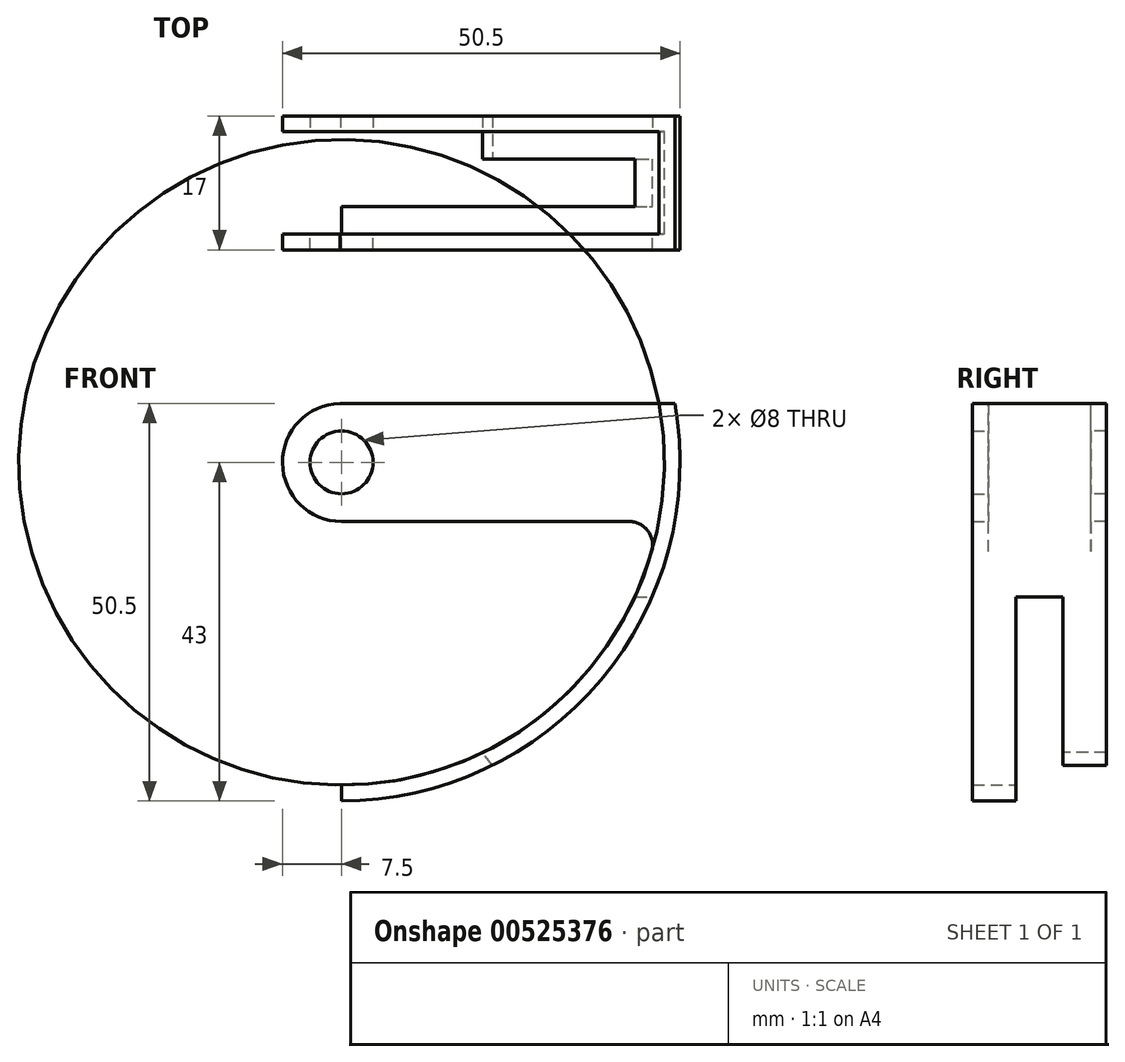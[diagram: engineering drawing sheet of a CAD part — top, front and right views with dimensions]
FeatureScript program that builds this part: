
annotation { "Feature Type Name" : "Feature", "Feature Type Description" : "" }
export const myFeature = defineFeature(function(context is Context, id is Id, definition is map)
    precondition{}
    {
        {
            var Q0;
            Q0=qCreatedBy(makeId("Front.planeOp"),FACE);
            var sketch = newSketch(context, id + "F0", { "sketchPlane" : qUnion([Q0])});
            skCircle(sketch, "E0", {"center": v(0, 0) * mm, "radius": 7.5 * mm});
            skLineSegment(sketch, "E1", {"start": v(0, 7.5) * mm, "end": v(42.34, 7.5) * mm});
            skLineSegment(sketch, "E2", {"start": v(0, -17) * mm, "end": v(32.65, -17) * mm});
            skLineSegment(sketch, "E3", {"start": v(37.28, -17.06) * mm, "end": v(39.47, -17.06) * mm});
            skArc(sketch, "E4", {"start": v(40.3, 7.5) * mm, "mid": v(-40.7, 5.02) * mm, "end": v(37.28, -17.06) * mm});
            skArc(sketch, "E5", {"start": v(37.28, -17.06) * mm, "mid": v(40.7, -5.02) * mm, "end": v(40.3, 7.5) * mm});
            skArc(sketch, "E6", {"start": v(39.47, -17.06) * mm, "mid": v(42.7, -5) * mm, "end": v(42.34, 7.5) * mm});
            skArc(sketch, "E7", {"start": v(42.34, 7.5) * mm, "mid": v(-42.7, 5) * mm, "end": v(39.47, -17.06) * mm});
            skSolve(sketch);
        }
        {
            var Q0;
            Q0=makeQuery(id+"F0.imprint","IMPRINT",FACE,{"disambiguationData":[TD([[makeQuery(id+"F0.imprint","IMPRINT",EDGE,{"derivedFrom":sQuery(id+"F0.wireOp",EDGE,"E3")}),1.0]])]});
            extrude(context, id + "F1", {"entities" : qUnion([Q0]), "depth" : 3 * mm, "offsetDistance" : 25.4 * mm});
        }
        {
            var Q0;
            Q0=makeQuery(id+"F1.opExtrude","SWEPT_BODY",BODY,{"disambiguationData":[OSD([sQuery(id+"F0.wireOp",EDGE,"E1"),sQuery(id+"F0.wireOp",EDGE,"E3"),sQuery(id+"F0.wireOp",EDGE,"E5"),sQuery(id+"F0.wireOp",EDGE,"E6")])]});
            var Q1;
            Q1=qCreatedBy(makeId("Front.planeOp"),FACE);
            mirror(context, id + "F2", {"operationType" : NewBodyOperationType.ADD, "entities" : qUnion([Q0]), "mirrorPlane" : qUnion([Q1])});
        }
        {
            var Q0;
            Q0=makeQuery(id+"F1.opExtrude","CAP_FACE",FACE,{"disambiguationData":[OSD([sQuery(id+"F0.wireOp",EDGE,"E1"),sQuery(id+"F0.wireOp",EDGE,"E3"),sQuery(id+"F0.wireOp",EDGE,"E5"),sQuery(id+"F0.wireOp",EDGE,"E6")])],"isStart":false});
            var sketch = newSketch(context, id + "F3", { "sketchPlane" : qUnion([Q0])});
            skCircle(sketch, "E8", {"center": v(0, 0) * mm, "radius": 7.5 * mm});
            skLineSegment(sketch, "E9", {"start": v(0, 7.5) * mm, "end": v(42.34, 7.5) * mm});
            skLineSegment(sketch, "E10", {"start": v(-7.6, -13.58) * mm, "end": v(25.06, -13.58) * mm});
            skLineSegment(sketch, "E11", {"start": v(37.28, -17.06) * mm, "end": v(39.47, -17.06) * mm});
            skArc(sketch, "E12", {"start": v(40.3, 7.5) * mm, "mid": v(-40.7, 5.02) * mm, "end": v(37.28, -17.06) * mm});
            skArc(sketch, "E13", {"start": v(37.28, -17.06) * mm, "mid": v(40.7, -5.02) * mm, "end": v(40.3, 7.5) * mm});
            skArc(sketch, "E14", {"start": v(39.47, -17.06) * mm, "mid": v(42.7, -5) * mm, "end": v(42.34, 7.5) * mm});
            skArc(sketch, "E15", {"start": v(42.34, 7.5) * mm, "mid": v(-42.7, 5) * mm, "end": v(39.47, -17.06) * mm});
            skLineSegment(sketch, "E16", {"start": v(0, -41) * mm, "end": v(0, -43) * mm});
            skSolve(sketch);
        }
        {
            var Q0;
            {var subQ0=sQuery(id+"F3.wireOp",EDGE,"E11");Q0=makeQuery(id+"F3.imprint","IMPRINT",FACE,{"disambiguationData":[TD([[makeQuery(id+"F3.imprint","IMPRINT",EDGE,{"derivedFrom":subQ0}),-1.0]])]});}
            var Q1;
            Q1=makeQuery(id+"F3.imprint","IMPRINT",FACE,{"disambiguationData":[TD([[makeQuery(id+"F3.imprint","IMPRINT",EDGE,{"derivedFrom":sQuery(id+"F3.wireOp",EDGE,"E11")}),1.0]])]});
            extrude(context, id + "F4", {"entities" : qUnion([Q0, Q1]), "operationType" : NewBodyOperationType.ADD, "depth" : 3.5 * mm, "offsetDistance" : 25.4 * mm});
        }
        {
            var Q0;
            Q0=makeQuery(id+"F4.opExtrude","CAP_FACE",FACE,{"disambiguationData":[OSD([sQuery(id+"F3.wireOp",EDGE,"E9"),sQuery(id+"F3.wireOp",EDGE,"E12"),sQuery(id+"F3.wireOp",EDGE,"E13"),sQuery(id+"F3.wireOp",EDGE,"E14"),sQuery(id+"F3.wireOp",EDGE,"E15"),sQuery(id+"F3.wireOp",EDGE,"E16")])],"isStart":false});
            var sketch = newSketch(context, id + "F5", { "sketchPlane" : qUnion([Q0])});
            skArc(sketch, "E17", {"start": v(37.28, -17.06) * mm, "mid": v(38.45, -14.24) * mm, "end": v(39.4, -11.33) * mm});
            skArc(sketch, "E18", {"start": v(39.47, -17.06) * mm, "mid": v(42.7, -5) * mm, "end": v(42.34, 7.5) * mm});
            skLineSegment(sketch, "E19", {"start": v(0, -7.5) * mm, "end": v(36.52, -7.5) * mm});
            skArc(sketch, "E20", {"start": v(-0.2, 7.5) * mm, "mid": v(-7.5, -0.1) * mm, "end": v(0, -7.5) * mm});
            skCircle(sketch, "E21", {"center": v(0, 0) * mm, "radius": 4 * mm});
            skLineSegment(sketch, "E22", {"start": v(40.3, -7.5) * mm, "end": v(40.3, -7.5) * mm});
            skArc(sketch, "E23.filletArc", {"start": v(39.4, -11.33) * mm, "mid": v(38.92, -8.7) * mm, "end": v(36.52, -7.5) * mm});
            skArc(sketch, "E24", {"start": v(0, -41) * mm, "mid": v(22.15, -34.5) * mm, "end": v(37.28, -17.06) * mm});
            skArc(sketch, "E25", {"start": v(0, -43) * mm, "mid": v(23.61, -35.94) * mm, "end": v(39.47, -17.06) * mm});
            skLineSegment(sketch, "E26", {"start": v(0, -41) * mm, "end": v(0, -43) * mm});
            skLineSegment(sketch, "E27", {"start": v(-0.2, 7.5) * mm, "end": v(42.34, 7.5) * mm});
            skSolve(sketch);
        }
        {
            var Q0;
            Q0=makeQuery(id+"F5.imprint","IMPRINT",FACE,{"disambiguationData":[TD([[makeQuery(id+"F5.imprint","IMPRINT",EDGE,{"derivedFrom":sQuery(id+"F5.wireOp",EDGE,"E19")}),1.0]])]});
            var Q1;
            {var subQ1=sQuery(id+"F5.wireOp",EDGE,"E17");Q1=makeQuery(id+"F5.imprint","IMPRINT",FACE,{"disambiguationData":[TD([[makeQuery(id+"F5.imprint","IMPRINT",EDGE,{"derivedFrom":subQ1}),-1.0]])]});}
            extrude(context, id + "F6", {"entities" : qUnion([Q0, Q1]), "operationType" : NewBodyOperationType.ADD, "depth" : 2 * mm, "offsetDistance" : 25.4 * mm});
        }
        {
            var Q0;
            Q0=makeQuery(id+"F2.opPattern","COPY",FACE,{"derivedFrom":makeQuery(id+"F1.opExtrude","CAP_FACE",FACE,{"disambiguationData":[OSD([sQuery(id+"F0.wireOp",EDGE,"E1"),sQuery(id+"F0.wireOp",EDGE,"E3"),sQuery(id+"F0.wireOp",EDGE,"E5"),sQuery(id+"F0.wireOp",EDGE,"E6")])],"isStart":false}),"instanceName":"1"});
            var sketch = newSketch(context, id + "F7", { "sketchPlane" : qUnion([Q0])});
            skLineSegment(sketch, "E28", {"start": v(-42.34, 7.5) * mm, "end": v(-40.3, 7.5) * mm});
            skLineSegment(sketch, "E29", {"start": v(-19.17, -38.5) * mm, "end": v(-17.93, -36.87) * mm});
            skArc(sketch, "E30", {"start": v(-42.36, 7.4) * mm, "mid": v(-38.38, -19.4) * mm, "end": v(-19.17, -38.5) * mm});
            skArc(sketch, "E31", {"start": v(-40.3, 7.53) * mm, "mid": v(-36.61, -18.45) * mm, "end": v(-17.93, -36.87) * mm});
            skLineSegment(sketch, "E32", {"start": v(-42.36, 7.4) * mm, "end": v(-42.34, 7.5) * mm});
            skSolve(sketch);
        }
        {
            var Q0;
            {var subQ3=sQuery(id+"F7.wireOp",EDGE,"E28");Q0=makeQuery(id+"F7.imprint","IMPRINT",FACE,{"disambiguationData":[TD([[makeQuery(id+"F7.imprint","IMPRINT",EDGE,{"derivedFrom":subQ3}),1.0]])]});}
            var Q1;
            {var subQ0=sQuery(id+"F7.wireOp",EDGE,"E29");Q1=makeQuery(id+"F7.imprint","IMPRINT",FACE,{"disambiguationData":[TD([[makeQuery(id+"F7.imprint","IMPRINT",EDGE,{"derivedFrom":subQ0}),1.0]])]});}
            extrude(context, id + "F8", {"entities" : qUnion([Q0, Q1]), "operationType" : NewBodyOperationType.ADD, "depth" : 3.5 * mm, "offsetDistance" : 25.4 * mm});
        }
        {
            var Q0;
            Q0=makeQuery(id+"F8.opExtrude","CAP_FACE",FACE,{"disambiguationData":[OSD([sQuery(id+"F7.wireOp",EDGE,"E28"),sQuery(id+"F7.wireOp",EDGE,"E29"),sQuery(id+"F7.wireOp",EDGE,"E30"),sQuery(id+"F7.wireOp",EDGE,"E31"),sQuery(id+"F7.wireOp",EDGE,"E32")])],"isStart":false});
            var sketch = newSketch(context, id + "F9", { "sketchPlane" : qUnion([Q0])});
            skLineSegment(sketch, "E33", {"start": v(-42.34, 7.5) * mm, "end": v(-40.3, 7.5) * mm});
            skLineSegment(sketch, "E34", {"start": v(-19.17, -38.5) * mm, "end": v(-17.93, -36.87) * mm});
            skArc(sketch, "E35", {"start": v(-42.36, 7.4) * mm, "mid": v(-38.38, -19.4) * mm, "end": v(-19.17, -38.5) * mm});
            skLineSegment(sketch, "E36", {"start": v(-42.36, 7.4) * mm, "end": v(-42.34, 7.5) * mm});
            skCircle(sketch, "E37", {"center": v(0, 0) * mm, "radius": 4 * mm});
            skArc(sketch, "E38", {"start": v(0.11, -7.5) * mm, "mid": v(7.5, 0.05) * mm, "end": v(0, 7.5) * mm});
            skLineSegment(sketch, "E39", {"start": v(0.11, -7.5) * mm, "end": v(-36.52, -7.5) * mm});
            skLineSegment(sketch, "E40", {"start": v(-39.4, -11.33) * mm, "end": v(-39.4, -11.33) * mm});
            skPoint(sketch, "E41.visualSharp", {"position": v(-40.3, -7.5) * mm});
            skArc(sketch, "E41.filletArc", {"start": v(-36.52, -7.5) * mm, "mid": v(-38.92, -8.7) * mm, "end": v(-39.4, -11.33) * mm});
            skArc(sketch, "E42", {"start": v(-39.4, -11.33) * mm, "mid": v(-31.38, -26.38) * mm, "end": v(-17.93, -36.87) * mm});
            skArc(sketch, "E43", {"start": v(-42.34, 7.5) * mm, "mid": v(-38.4, -19.35) * mm, "end": v(-19.16, -38.5) * mm});
            skLineSegment(sketch, "E44", {"start": v(-40.3, 7.5) * mm, "end": v(0, 7.5) * mm});
            skSolve(sketch);
        }
        {
            var Q0;
            Q0=makeQuery(id+"F9.imprint","IMPRINT",FACE,{"disambiguationData":[TD([[makeQuery(id+"F9.imprint","IMPRINT",EDGE,{"derivedFrom":sQuery(id+"F9.wireOp",EDGE,"E37")}),-1.0]])]});
            var Q1;
            {var subQ1=sQuery(id+"F9.wireOp",EDGE,"E33");Q1=makeQuery(id+"F9.imprint","IMPRINT",FACE,{"disambiguationData":[TD([[makeQuery(id+"F9.imprint","IMPRINT",EDGE,{"derivedFrom":subQ1}),1.0]])]});}
            extrude(context, id + "F10", {"entities" : qUnion([Q0, Q1]), "operationType" : NewBodyOperationType.ADD, "depth" : 2 * mm, "offsetDistance" : 25.4 * mm});
        }
    });
